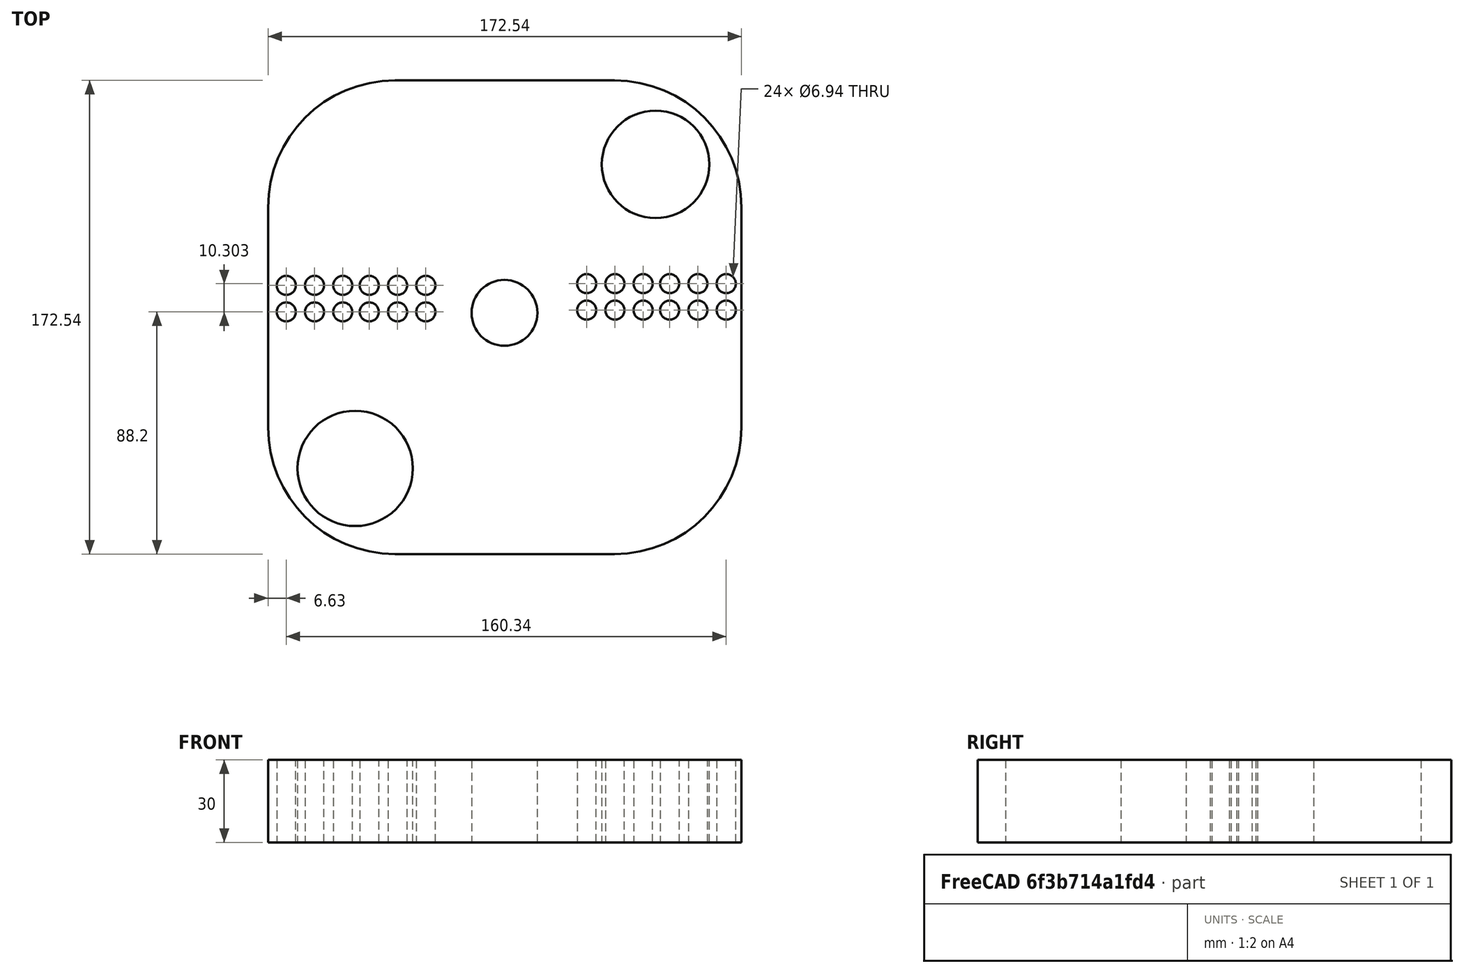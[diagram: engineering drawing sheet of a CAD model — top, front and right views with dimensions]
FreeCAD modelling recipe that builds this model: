
FCSTD DOCUMENT  (FreeCAD 0.18R16131 (Git))
Label: Momentum_Mold_Plate_1-1_160X200_12T_12mm(lm12uu)
License: All rights reserved
LicenseURL: http://en.wikipedia.org/wiki/All_rights_reserved
objects: PartDesign::Pad×2, Sketcher::SketchObject×1, PartDesign::Body×1
note: 6 computed .brp shape members not serialized (recipe doc carries the construction recipe); baked Part::Feature solids carry a one-line shape summary decoded from their .brp

FEATURE [Sketcher::SketchObject] Sketch
  MapMode = 5
  Support = -> [XY_Plane]
  sketch-geometry (35):
    g0: LineSegment StartX=-35.5842 StartY=-63.1111 StartZ=0 EndX=44.4158 EndY=-63.1111 EndZ=0
    g1: LineSegment StartX=90.685 StartY=-16.8419 StartZ=0 EndX=90.685 EndY=63.1581 EndZ=0
    g2: LineSegment StartX=44.4158 StartY=109.427 StartZ=0 EndX=-35.5842 EndY=109.427 EndZ=0
    g3: LineSegment StartX=-81.8534 StartY=63.1581 StartZ=0 EndX=-81.8534 EndY=-16.8419 EndZ=0
    g4: Circle CenterX=4.30636 CenterY=24.7677 CenterZ=0 NormalX=0 NormalY=0 NormalZ=1 AngleXU=0 Radius=12
    g5: Circle CenterX=-50.1062 CenterY=-31.8986 CenterZ=0 NormalX=0 NormalY=0 NormalZ=1 AngleXU=0 Radius=21
    g6: Circle CenterX=59.3629 CenterY=78.8583 CenterZ=0 NormalX=0 NormalY=0 NormalZ=1 AngleXU=0 Radius=19.5845
    g7: ArcOfCircle CenterX=-35.5842 CenterY=63.1581 CenterZ=0 NormalX=0 NormalY=0 NormalZ=1 AngleXU=0 Radius=46.2692 StartAngle=1.5708 EndAngle=3.14159
    g8: ArcOfCircle CenterX=44.4158 CenterY=63.1581 CenterZ=0 NormalX=0 NormalY=0 NormalZ=1 AngleXU=0 Radius=46.2692 StartAngle=1e-16 EndAngle=1.5708
    g9: ArcOfCircle CenterX=44.4158 CenterY=-16.8419 CenterZ=0 NormalX=0 NormalY=0 NormalZ=1 AngleXU=0 Radius=46.2692 StartAngle=4.71239 EndAngle=6.28319
    g10: ArcOfCircle CenterX=-35.5842 CenterY=-16.8419 CenterZ=0 NormalX=0 NormalY=0 NormalZ=1 AngleXU=0 Radius=46.2692 StartAngle=3.14159 EndAngle=4.71239
    g11: Circle CenterX=-75.2197 CenterY=34.7487 CenterZ=0 NormalX=0 NormalY=0 NormalZ=1 AngleXU=0 Radius=3.4677
    g12: Circle CenterX=-64.9167 CenterY=34.7487 CenterZ=0 NormalX=0 NormalY=0 NormalZ=1 AngleXU=0 Radius=3.4677
    g13: Circle CenterX=-54.6138 CenterY=34.7487 CenterZ=0 NormalX=0 NormalY=0 NormalZ=1 AngleXU=0 Radius=3.4677
    g14: Circle CenterX=-44.9547 CenterY=34.7487 CenterZ=0 NormalX=0 NormalY=0 NormalZ=1 AngleXU=0 Radius=3.4677
    g15: Circle CenterX=-34.6518 CenterY=34.7487 CenterZ=0 NormalX=0 NormalY=0 NormalZ=1 AngleXU=0 Radius=3.4677
    g16: Circle CenterX=-24.3488 CenterY=34.7487 CenterZ=0 NormalX=0 NormalY=0 NormalZ=1 AngleXU=0 Radius=3.4677
    g17: Circle CenterX=-75.2197 CenterY=25.0897 CenterZ=0 NormalX=0 NormalY=0 NormalZ=1 AngleXU=0 Radius=3.4677
    g18: Circle CenterX=-64.9167 CenterY=25.0897 CenterZ=0 NormalX=0 NormalY=0 NormalZ=1 AngleXU=0 Radius=3.4677
    g19: Circle CenterX=-54.6138 CenterY=25.0897 CenterZ=0 NormalX=0 NormalY=0 NormalZ=1 AngleXU=0 Radius=3.4677
    g20: Circle CenterX=-44.9547 CenterY=25.0897 CenterZ=0 NormalX=0 NormalY=0 NormalZ=1 AngleXU=0 Radius=3.4677
    g21: Circle CenterX=-34.6518 CenterY=25.0897 CenterZ=0 NormalX=0 NormalY=0 NormalZ=1 AngleXU=0 Radius=3.4677
    g22: Circle CenterX=-24.3488 CenterY=25.0897 CenterZ=0 NormalX=0 NormalY=0 NormalZ=1 AngleXU=0 Radius=3.4677
    g23: Circle CenterX=34.2494 CenterY=35.3926 CenterZ=0 NormalX=0 NormalY=0 NormalZ=1 AngleXU=0 Radius=3.4677
    g24: Circle CenterX=44.5523 CenterY=35.3926 CenterZ=0 NormalX=0 NormalY=0 NormalZ=1 AngleXU=0 Radius=3.4677
    g25: Circle CenterX=54.8553 CenterY=35.3926 CenterZ=0 NormalX=0 NormalY=0 NormalZ=1 AngleXU=0 Radius=3.4677
    g26: Circle CenterX=64.5144 CenterY=35.3926 CenterZ=0 NormalX=0 NormalY=0 NormalZ=1 AngleXU=0 Radius=3.4677
    g27: Circle CenterX=74.8173 CenterY=35.3926 CenterZ=0 NormalX=0 NormalY=0 NormalZ=1 AngleXU=0 Radius=3.4677
    g28: Circle CenterX=85.1203 CenterY=35.3926 CenterZ=0 NormalX=0 NormalY=0 NormalZ=1 AngleXU=0 Radius=3.4677
    g29: Circle CenterX=34.2494 CenterY=25.7336 CenterZ=0 NormalX=0 NormalY=0 NormalZ=1 AngleXU=0 Radius=3.4677
    g30: Circle CenterX=44.5523 CenterY=25.7336 CenterZ=0 NormalX=0 NormalY=0 NormalZ=1 AngleXU=0 Radius=3.4677
    g31: Circle CenterX=54.8553 CenterY=25.7336 CenterZ=0 NormalX=0 NormalY=0 NormalZ=1 AngleXU=0 Radius=3.4677
    g32: Circle CenterX=64.5144 CenterY=25.7336 CenterZ=0 NormalX=0 NormalY=0 NormalZ=1 AngleXU=0 Radius=3.4677
    g33: Circle CenterX=74.8173 CenterY=25.7336 CenterZ=0 NormalX=0 NormalY=0 NormalZ=1 AngleXU=0 Radius=3.4677
    g34: Circle CenterX=85.1203 CenterY=25.7336 CenterZ=0 NormalX=0 NormalY=0 NormalZ=1 AngleXU=0 Radius=3.4677
  constraints (39):
    c: Horizontal(g0)
    c: Horizontal(g2)
    c: Vertical(g1)
    c: Vertical(g3)
    c: Radius(g4) = 12
    c: Radius(g5) = 21
    c: Tangent(g2,g7) = -1.5708
    c: Tangent(g3,g7) = -1.5708
    c: Tangent(g2,g8) = -1.5708
    c: Tangent(g1,g8) = -1.5708
    c: Tangent(g1,g9) = -1.5708
    c: Tangent(g0,g9) = -1.5708
    c: Tangent(g0,g10) = -1.5708
    c: Tangent(g3,g10) = -1.5708
    c: Vertical(g7,g10)
    c: DistanceY(g1,g1) = 80
    c: DistanceY(g3,g3) = 80
    c: Horizontal(g1,g3)
    c: DistanceX(g2,g2) = 80
    c: Horizontal(g11,g12)
    c: Horizontal(g12,g13)
    c: Horizontal(g13,g14)
    c: Horizontal(g14,g15)
    c: Horizontal(g15,g16)
    c: Horizontal(g17,g18)
    c: Horizontal(g18,g19)
    c: Horizontal(g19,g20)
    c: Horizontal(g20,g21)
    c: Horizontal(g21,g22)
    c: Horizontal(g23,g24)
    c: Horizontal(g24,g25)
    c: Horizontal(g25,g26)
    c: Horizontal(g26,g27)
    c: Horizontal(g27,g28)
    c: Horizontal(g29,g30)
    c: Horizontal(g30,g31)
    c: Horizontal(g31,g32)
    c: Horizontal(g32,g33)
    c: Horizontal(g33,g34)
FEATURE [PartDesign::Pad] Pad
  Length = 30
  Length2 = 100
  Profile = -> Sketch
  Type = 0
FEATURE [PartDesign::Pad] Pad001
  BaseFeature = -> Pad
  Length = 30
  Length2 = 100
  Profile = -> Sketch
  Type = 0
FEATURE [PartDesign::Body] Body
  Group = -> [Sketch,Pad,Pad001]
  Origin = -> Origin
  Tip = -> Pad001
